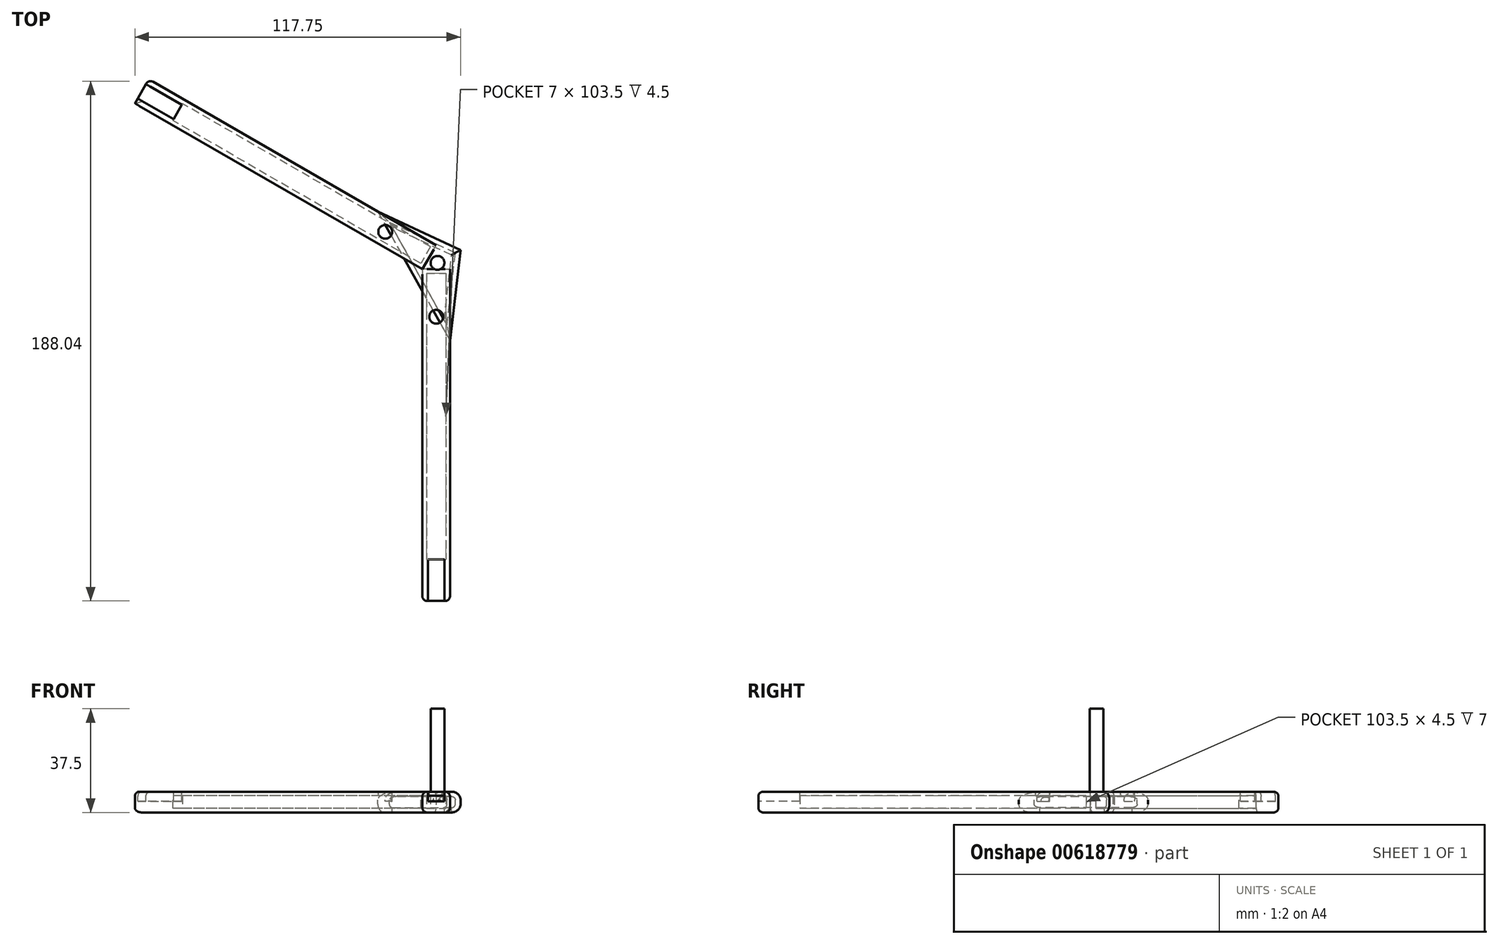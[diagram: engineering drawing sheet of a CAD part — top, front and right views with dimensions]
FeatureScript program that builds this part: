
annotation { "Feature Type Name" : "Feature", "Feature Type Description" : "" }
export const myFeature = defineFeature(function(context is Context, id is Id, definition is map)
    precondition{}
    {
        {
            var Q0;
            Q0=qCreatedBy(makeId("Top.planeOp"),FACE);
            var sketch = newSketch(context, id + "F0", { "sketchPlane" : qUnion([Q0])});
            skLineSegment(sketch, "E0.bottom", {"start": v(-40.03, 61.48) * mm, "end": v(-30.03, 61.48) * mm});
            skLineSegment(sketch, "E0.top", {"start": v(-40.03, -58.52) * mm, "end": v(-30.03, -58.52) * mm});
            skLineSegment(sketch, "E0.left", {"start": v(-40.03, 61.48) * mm, "end": v(-40.03, -58.52) * mm});
            skLineSegment(sketch, "E0.right", {"start": v(-30.03, 61.48) * mm, "end": v(-30.03, -58.52) * mm});
            skSolve(sketch);
        }
        {
            var Q0;
            Q0=makeQuery(id+"F0.imprint","IMPRINT",FACE,{"disambiguationData":[TD([[makeQuery(id+"F0.imprint","IMPRINT",EDGE,{"derivedFrom":sQuery(id+"F0.wireOp",EDGE,"E0.bottom")}),-1.0]])]});
            extrude(context, id + "F1", {"entities" : qUnion([Q0]), "depth" : 7.5 * mm, "offsetDistance" : 25 * mm});
        }
        {
            var Q0;
            Q0=makeQuery(id+"F1.opExtrude","SWEPT_BODY",BODY,{"disambiguationData":[OSD([sQuery(id+"F0.wireOp",EDGE,"E0.bottom"),sQuery(id+"F0.wireOp",EDGE,"E0.top"),sQuery(id+"F0.wireOp",EDGE,"E0.left"),sQuery(id+"F0.wireOp",EDGE,"E0.right")])]});
            var Q1;
            Q1=makeQuery(id+"F1.opExtrude","SWEPT_EDGE",EDGE,{"disambiguationData":[OSD([sQuery(id+"F0.wireOp",EDGE,"E0.bottom"),sQuery(id+"F0.wireOp",EDGE,"E0.left")])]});
            circularPattern(context, id + "F2", {"entities" : qUnion([Q0]), "axis" : qUnion([Q1]), "angle" : 120 * degree, "instanceCount" : 2, "equalSpace" : true});
        }
        {
            var Q0;
            Q0=makeQuery(id+"F2.opPattern","COPY",FACE,{"derivedFrom":makeQuery(id+"F1.opExtrude","CAP_FACE",FACE,{"disambiguationData":[OSD([sQuery(id+"F0.wireOp",EDGE,"E0.bottom"),sQuery(id+"F0.wireOp",EDGE,"E0.top"),sQuery(id+"F0.wireOp",EDGE,"E0.left"),sQuery(id+"F0.wireOp",EDGE,"E0.right")])],"isStart":false}),"instanceName":"1"});
            var sketch = newSketch(context, id + "F3", { "sketchPlane" : qUnion([Q0])});
            skSolve(sketch);
        }
        {
            var Q0;
            Q0 = qSketchRegion(id + "F3", true);
            var Q1;
            Q1=makeQuery(id+"F2.opPattern","COPY",FACE,{"derivedFrom":makeQuery(id+"F1.opExtrude","SWEPT_FACE",FACE,{"disambiguationData":[OSD([sQuery(id+"F0.wireOp",EDGE,"E0.left")])]}),"instanceName":"1"});
            extrude(context, id + "F4", {"entities" : qUnion([Q0, Q1]), "operationType" : NewBodyOperationType.ADD, "depth" : 10 * mm, "offsetDistance" : 25 * mm});
        }
        {
            var Q0;
            Q0=makeQuery(id+"F3.imprint","IMPRINT",FACE,{"disambiguationData":[TD([[makeQuery(id+"F3.imprint","IMPRINT",EDGE,{"derivedFrom":makeQuery(id+"F2.opPattern","COPY",EDGE,{"derivedFrom":makeQuery(id+"F1.opExtrude","CAP_EDGE",EDGE,{"disambiguationData":[OSD([sQuery(id+"F0.wireOp",EDGE,"E0.bottom")])],"isStart":false}),"instanceName":"1"})}),-1.0]])]});
            extrude(context, id + "F5", {"entities" : qUnion([Q0]), "operationType" : NewBodyOperationType.REMOVE, "endBound" : BoundingType.THROUGH_ALL, "oppositeDirection" : true, "depth" : 25 * mm, "offsetDistance" : 25 * mm});
        }
        {
            var Q0;
            Q0=makeQuery(id+"F1.opExtrude","CAP_FACE",FACE,{"disambiguationData":[OSD([sQuery(id+"F0.wireOp",EDGE,"E0.bottom"),sQuery(id+"F0.wireOp",EDGE,"E0.top"),sQuery(id+"F0.wireOp",EDGE,"E0.left"),sQuery(id+"F0.wireOp",EDGE,"E0.right")])],"isStart":false});
            var sketch = newSketch(context, id + "F6", { "sketchPlane" : qUnion([Q0])});
            skLineSegment(sketch, "E1", {"start": v(-30.03, 35.65) * mm, "end": v(-26.2, 68.43) * mm});
            skLineSegment(sketch, "E2", {"start": v(-26.2, 68.43) * mm, "end": v(-56.14, 82.33) * mm});
            skLineSegment(sketch, "E3", {"start": v(-56.14, 82.33) * mm, "end": v(-30.03, 35.65) * mm});
            skSolve(sketch);
        }
        {
            var Q0;
            Q0=makeQuery(id+"F1.opExtrude","SWEPT_FACE",FACE,{"disambiguationData":[OSD([sQuery(id+"F0.wireOp",EDGE,"E0.top")])]});
            shell(context, id + "F7", {"entities" : qUnion([Q0]), "thickness" : 1.5 * mm});
        }
        {
            var Q0;
            {var subQ0=sQuery(id+"F0.wireOp",EDGE,"E0.top");Q0=makeQuery(id+"F4.boolean.opBoolean","MERGE",FACE,{"derivedFrom":[makeQuery(id+"F2.opPattern","COPY",FACE,{"derivedFrom":makeQuery(id+"F1.opExtrude","SWEPT_FACE",FACE,{"disambiguationData":[OSD([subQ0])]}),"instanceName":"1"}),makeQuery(id+"F4.opExtrude","SWEPT_FACE",FACE,{"disambiguationData":[OSD([subQ0,sQuery(id+"F0.wireOp",EDGE,"E0.left")])]})]});}
            shell(context, id + "F8", {"entities" : qUnion([Q0]), "thickness" : 1.5 * mm});
        }
        {
            var Q0;
            {var subQ0=sQuery(id+"F0.wireOp",EDGE,"E0.top");Q0=makeQuery(id+"F4.boolean.opBoolean","MERGE",FACE,{"derivedFrom":[makeQuery(id+"F2.opPattern","COPY",FACE,{"derivedFrom":makeQuery(id+"F1.opExtrude","SWEPT_FACE",FACE,{"disambiguationData":[OSD([subQ0])]}),"instanceName":"1"}),makeQuery(id+"F4.opExtrude","SWEPT_FACE",FACE,{"disambiguationData":[OSD([subQ0,sQuery(id+"F0.wireOp",EDGE,"E0.left")])]})]});}
            var sketch = newSketch(context, id + "F9", { "sketchPlane" : qUnion([Q0])});
            skLineSegment(sketch, "E4", {"start": v(-41.73, 6) * mm, "end": v(-34.73, 6) * mm});
            skLineSegment(sketch, "E5", {"start": v(-34.73, 6) * mm, "end": v(-34.73, 1.5) * mm});
            skLineSegment(sketch, "E6", {"start": v(-34.73, 1.5) * mm, "end": v(-41.73, 1.5) * mm});
            skLineSegment(sketch, "E7", {"start": v(-41.73, 1.5) * mm, "end": v(-41.73, 6) * mm});
            skSolve(sketch);
        }
        {
            var Q0;
            Q0=makeQuery(id+"F9.imprint","IMPRINT",FACE,{"disambiguationData":[TD([[makeQuery(id+"F9.imprint","IMPRINT",EDGE,{"derivedFrom":sQuery(id+"F9.wireOp",EDGE,"E4")}),-1.0]])]});
            extrude(context, id + "F10", {"entities" : qUnion([Q0]), "operationType" : NewBodyOperationType.ADD, "oppositeDirection" : true, "depth" : 15 * mm, "offsetDistance" : 25 * mm});
        }
        {
            var Q0;
            Q0=makeQuery(id+"F1.opExtrude","SWEPT_FACE",FACE,{"disambiguationData":[OSD([sQuery(id+"F0.wireOp",EDGE,"E0.top")])]});
            var sketch = newSketch(context, id + "F11", { "sketchPlane" : qUnion([Q0])});
            skLineSegment(sketch, "E8", {"start": v(-38.53, 6) * mm, "end": v(-31.53, 6) * mm});
            skLineSegment(sketch, "E9", {"start": v(-31.53, 6) * mm, "end": v(-31.53, 1.5) * mm});
            skLineSegment(sketch, "E10", {"start": v(-31.53, 1.5) * mm, "end": v(-38.53, 1.5) * mm});
            skLineSegment(sketch, "E11", {"start": v(-38.53, 1.5) * mm, "end": v(-38.53, 6) * mm});
            skSolve(sketch);
        }
        {
            var Q0;
            Q0=makeQuery(id+"F11.imprint","IMPRINT",FACE,{"disambiguationData":[TD([[makeQuery(id+"F11.imprint","IMPRINT",EDGE,{"derivedFrom":sQuery(id+"F11.wireOp",EDGE,"E8")}),-1.0]])]});
            var Q1;
            Q1=makeQuery(id+"F11.imprint","IMPRINT",FACE,{"disambiguationData":[TD([[makeQuery(id+"F11.imprint","IMPRINT",EDGE,{"derivedFrom":sQuery(id+"F11.wireOp",EDGE,"E8")}),1.0]])]});
            extrude(context, id + "F12", {"entities" : qUnion([Q0, Q1]), "operationType" : NewBodyOperationType.ADD, "oppositeDirection" : true, "depth" : 15 * mm, "offsetDistance" : 25 * mm});
        }
        {
            var Q0;
            Q0=makeQuery(id+"F1.opExtrude","CAP_EDGE",EDGE,{"disambiguationData":[OSD([sQuery(id+"F0.wireOp",EDGE,"E0.left")])],"isStart":false});
            var Q1;
            Q1=makeQuery(id+"F1.opExtrude","CAP_EDGE",EDGE,{"disambiguationData":[OSD([sQuery(id+"F0.wireOp",EDGE,"E0.top")])],"isStart":false});
            var Q2;
            Q2=makeQuery(id+"F1.opExtrude","CAP_EDGE",EDGE,{"disambiguationData":[OSD([sQuery(id+"F0.wireOp",EDGE,"E0.right")])],"isStart":false});
            var Q3;
            {var subQ0=sQuery(id+"F0.wireOp",EDGE,"E0.left");Q3=makeQuery(id+"F4.opExtrude","CAP_EDGE",EDGE,{"disambiguationData":[OSD([subQ0]),TDD([makeQuery(id+"F2.opPattern","COPY",EDGE,{"derivedFrom":makeQuery(id+"F1.opExtrude","CAP_EDGE",EDGE,{"disambiguationData":[OSD([subQ0])],"isStart":false}),"instanceName":"1"})])],"isStart":false});}
            var Q4;
            Q4=makeQuery(id+"F5.boolean.opBoolean","COPY",EDGE,{"derivedFrom":makeQuery(id+"F5.opExtrude","CAP_EDGE",EDGE,{"disambiguationData":[OSD([sQuery(id+"F0.wireOp",EDGE,"E0.left")])],"isStart":true})});
            var Q5;
            {var subQ0=sQuery(id+"F0.wireOp",EDGE,"E0.left");var subQ1=sQuery(id+"F0.wireOp",EDGE,"E0.top");Q5=makeQuery(id+"F4.boolean.opBoolean","MERGE",EDGE,{"derivedFrom":[makeQuery(id+"F2.opPattern","COPY",EDGE,{"derivedFrom":makeQuery(id+"F1.opExtrude","CAP_EDGE",EDGE,{"disambiguationData":[OSD([subQ1])],"isStart":false}),"instanceName":"1"}),makeQuery(id+"F4.opExtrude","SWEPT_EDGE",EDGE,{"disambiguationData":[OSD([subQ1,subQ0]),TDD([makeQuery(id+"F2.opPattern","COPY",VERTEX,{"derivedFrom":makeQuery(id+"F1.opExtrude","CAP_VERTEX",VERTEX,{"disambiguationData":[OSD([subQ1,subQ0])],"isStart":false}),"instanceName":"1"})])]})]});}
            var Q6;
            Q6=makeQuery(id+"F5.boolean.opBoolean","COPY",EDGE,{"derivedFrom":makeQuery(id+"F5.opExtrude","SWEPT_EDGE",EDGE,{"disambiguationData":[OSD([sQuery(id+"F0.wireOp",EDGE,"E0.top"),sQuery(id+"F0.wireOp",EDGE,"E0.left")])]})});
            var Q7;
            Q7=makeQuery(id+"F4.opExtrude","CAP_EDGE",EDGE,{"disambiguationData":[OSD([sQuery(id+"F0.wireOp",EDGE,"E0.top"),sQuery(id+"F0.wireOp",EDGE,"E0.left")])],"isStart":false});
            var Q8;
            {var subQ0=sQuery(id+"F0.wireOp",EDGE,"E0.left");var subQ1=sQuery(id+"F0.wireOp",EDGE,"E0.top");Q8=makeQuery(id+"F4.boolean.opBoolean","MERGE",EDGE,{"derivedFrom":[makeQuery(id+"F2.opPattern","COPY",EDGE,{"derivedFrom":makeQuery(id+"F1.opExtrude","CAP_EDGE",EDGE,{"disambiguationData":[OSD([subQ1])],"isStart":true}),"instanceName":"1"}),makeQuery(id+"F4.opExtrude","SWEPT_EDGE",EDGE,{"disambiguationData":[OSD([subQ1,subQ0]),TDD([makeQuery(id+"F2.opPattern","COPY",VERTEX,{"derivedFrom":makeQuery(id+"F1.opExtrude","CAP_VERTEX",VERTEX,{"disambiguationData":[OSD([subQ1,subQ0])],"isStart":true}),"instanceName":"1"})])]})]});}
            var Q9;
            {var subQ0=sQuery(id+"F0.wireOp",EDGE,"E0.left");Q9=makeQuery(id+"F4.opExtrude","CAP_EDGE",EDGE,{"disambiguationData":[OSD([subQ0]),TDD([makeQuery(id+"F2.opPattern","COPY",EDGE,{"derivedFrom":makeQuery(id+"F1.opExtrude","CAP_EDGE",EDGE,{"disambiguationData":[OSD([subQ0])],"isStart":true}),"instanceName":"1"})])],"isStart":false});}
            var Q10;
            Q10=makeQuery(id+"F1.opExtrude","CAP_EDGE",EDGE,{"disambiguationData":[OSD([sQuery(id+"F0.wireOp",EDGE,"E0.right")])],"isStart":true});
            var Q11;
            Q11=makeQuery(id+"F1.opExtrude","CAP_EDGE",EDGE,{"disambiguationData":[OSD([sQuery(id+"F0.wireOp",EDGE,"E0.left")])],"isStart":true});
            var Q12;
            Q12=makeQuery(id+"F1.opExtrude","CAP_EDGE",EDGE,{"disambiguationData":[OSD([sQuery(id+"F0.wireOp",EDGE,"E0.top")])],"isStart":true});
            var Q13;
            Q13=makeQuery(id+"F1.opExtrude","SWEPT_EDGE",EDGE,{"disambiguationData":[OSD([sQuery(id+"F0.wireOp",EDGE,"E0.top"),sQuery(id+"F0.wireOp",EDGE,"E0.right")])]});
            var Q14;
            Q14=makeQuery(id+"F1.opExtrude","SWEPT_EDGE",EDGE,{"disambiguationData":[OSD([sQuery(id+"F0.wireOp",EDGE,"E0.top"),sQuery(id+"F0.wireOp",EDGE,"E0.left")])]});
            var Q15;
            {var subQ0=sQuery(id+"F0.wireOp",EDGE,"E0.left");Q15=makeQuery(id+"F5.boolean.opBoolean","INTERSECT",EDGE,{"derivedFrom":[makeQuery(id+"F4.boolean.opBoolean","MERGE",FACE,{"derivedFrom":[makeQuery(id+"F2.opPattern","COPY",FACE,{"derivedFrom":makeQuery(id+"F1.opExtrude","CAP_FACE",FACE,{"disambiguationData":[OSD([sQuery(id+"F0.wireOp",EDGE,"E0.bottom"),sQuery(id+"F0.wireOp",EDGE,"E0.top"),subQ0,sQuery(id+"F0.wireOp",EDGE,"E0.right")])],"isStart":true}),"instanceName":"1"}),makeQuery(id+"F4.opExtrude","SWEPT_FACE",FACE,{"disambiguationData":[OSD([subQ0]),TDD([makeQuery(id+"F2.opPattern","COPY",EDGE,{"derivedFrom":makeQuery(id+"F1.opExtrude","CAP_EDGE",EDGE,{"disambiguationData":[OSD([subQ0])],"isStart":true}),"instanceName":"1"})])]})]}),makeQuery(id+"F5.opExtrude","SWEPT_FACE",FACE,{"disambiguationData":[OSD([subQ0])]})]});}
            fillet(context, id + "F13", {"entities" : qUnion([Q0, Q1, Q2, Q3, Q4, Q5, Q6, Q7, Q8, Q9, Q10, Q11, Q12, Q13, Q14, Q15]), "radius" : 1.7 * mm, "tangentPropagation" : true, "allowEdgeOverflow" : false});
        }
        {
            var Q0;
            {var subQ5=sQuery(id+"F6.wireOp",EDGE,"E1");Q0=makeQuery(id+"F6.imprint","IMPRINT",FACE,{"disambiguationData":[TD([[makeQuery(id+"F6.imprint","IMPRINT",EDGE,{"derivedFrom":subQ5}),1.0]])]});}
            var Q1;
            {var subQ5=makeQuery(id+"F1.opExtrude","CAP_EDGE",EDGE,{"disambiguationData":[OSD([sQuery(id+"F0.wireOp",EDGE,"E0.bottom")])],"isStart":false});Q1=makeQuery(id+"F6.imprint","IMPRINT",FACE,{"disambiguationData":[TD([[makeQuery(id+"F6.imprint","IMPRINT",EDGE,{"derivedFrom":subQ5}),-1.0]])]});}
            extrude(context, id + "F14", {"entities" : qUnion([Q0, Q1]), "oppositeDirection" : true, "depth" : 7.5 * mm, "offsetDistance" : 25 * mm});
        }
        {
            var Q0;
            Q0=makeQuery(id+"F14.opExtrude","CAP_EDGE",EDGE,{"disambiguationData":[OSD([sQuery(id+"F6.wireOp",EDGE,"E1")])],"isStart":true});
            var Q1;
            Q1=makeQuery(id+"F14.opExtrude","CAP_EDGE",EDGE,{"disambiguationData":[OSD([sQuery(id+"F6.wireOp",EDGE,"E1")])],"isStart":false});
            var Q2;
            Q2=makeQuery(id+"F14.opExtrude","CAP_EDGE",EDGE,{"disambiguationData":[OSD([sQuery(id+"F6.wireOp",EDGE,"E2")])],"isStart":false});
            var Q3;
            Q3=makeQuery(id+"F14.opExtrude","CAP_EDGE",EDGE,{"disambiguationData":[OSD([sQuery(id+"F6.wireOp",EDGE,"E2")])],"isStart":true});
            var Q4;
            Q4=makeQuery(id+"F14.opExtrude","CAP_EDGE",EDGE,{"disambiguationData":[OSD([sQuery(id+"F6.wireOp",EDGE,"E3")])],"isStart":true});
            fillet(context, id + "F15", {"entities" : qUnion([Q0, Q1, Q2, Q3, Q4]), "radius" : 3 * mm, "tangentPropagation" : true, "allowEdgeOverflow" : false});
        }
        {
            var Q0;
            Q0=makeQuery(id+"F14.opExtrude","CAP_FACE",FACE,{"disambiguationData":[OSD([sQuery(id+"F6.wireOp",EDGE,"E1"),sQuery(id+"F6.wireOp",EDGE,"E2"),sQuery(id+"F6.wireOp",EDGE,"E3")])],"isStart":false});
            shell(context, id + "F16", {"entities" : qUnion([Q0]), "thickness" : 1.75 * mm});
        }
        {
            var Q0;
            Q0=makeQuery(id+"F14.opExtrude","CAP_FACE",FACE,{"disambiguationData":[OSD([sQuery(id+"F6.wireOp",EDGE,"E1"),sQuery(id+"F6.wireOp",EDGE,"E2"),sQuery(id+"F6.wireOp",EDGE,"E3")])],"isStart":true});
            var sketch = newSketch(context, id + "F17", { "sketchPlane" : qUnion([Q0])});
            skCircle(sketch, "E12", {"center": v(-34.54, 63.77) * mm, "radius": 2.5 * mm});
            skSolve(sketch);
        }
        {
            var Q0;
            Q0=makeQuery(id+"F17.imprint","IMPRINT",FACE,{"disambiguationData":[TD([[makeQuery(id+"F17.imprint","IMPRINT",EDGE,{"derivedFrom":sQuery(id+"F17.wireOp",EDGE,"E12")}),1.0]])]});
            extrude(context, id + "F18", {"entities" : qUnion([Q0]), "depth" : 30 * mm, "offsetDistance" : 25 * mm});
        }
        {
            var Q0;
            Q0=makeQuery(id+"F1.opExtrude","CAP_FACE",FACE,{"disambiguationData":[OSD([sQuery(id+"F0.wireOp",EDGE,"E0.bottom"),sQuery(id+"F0.wireOp",EDGE,"E0.top"),sQuery(id+"F0.wireOp",EDGE,"E0.left"),sQuery(id+"F0.wireOp",EDGE,"E0.right")])],"isStart":false});
            var sketch = newSketch(context, id + "F19", { "sketchPlane" : qUnion([Q0])});
            skLineSegment(sketch, "E13", {"start": v(-32.03, -58.52) * mm, "end": v(-32.03, -43.52) * mm});
            skLineSegment(sketch, "E14", {"start": v(-32.03, -43.52) * mm, "end": v(-38.03, -43.52) * mm});
            skLineSegment(sketch, "E15", {"start": v(-38.03, -43.52) * mm, "end": v(-38.03, -58.52) * mm});
            skLineSegment(sketch, "E16", {"start": v(-38.03, -58.52) * mm, "end": v(-32.03, -58.52) * mm});
            skSolve(sketch);
        }
        {
            var Q0;
            {var subQ0=sQuery(id+"F19.wireOp",EDGE,"E14");Q0=makeQuery(id+"F19.imprint","IMPRINT",FACE,{"disambiguationData":[TD([[makeQuery(id+"F19.imprint","IMPRINT",EDGE,{"derivedFrom":subQ0}),1.0]])]});}
            var Q1;
            {var subQ0=sQuery(id+"F19.wireOp",EDGE,"E16");Q1=makeQuery(id+"F19.imprint","IMPRINT",FACE,{"disambiguationData":[TD([[makeQuery(id+"F19.imprint","IMPRINT",EDGE,{"derivedFrom":subQ0}),1.0]])]});}
            extrude(context, id + "F20", {"entities" : qUnion([Q0, Q1]), "operationType" : NewBodyOperationType.REMOVE, "oppositeDirection" : true, "depth" : 3.5 * mm, "offsetDistance" : 25 * mm});
        }
        {
            var Q0;
            {var subQ0=sQuery(id+"F0.wireOp",EDGE,"E0.left");Q0=makeQuery(id+"F4.boolean.opBoolean","MERGE",FACE,{"derivedFrom":[makeQuery(id+"F2.opPattern","COPY",FACE,{"derivedFrom":makeQuery(id+"F1.opExtrude","CAP_FACE",FACE,{"disambiguationData":[OSD([sQuery(id+"F0.wireOp",EDGE,"E0.bottom"),sQuery(id+"F0.wireOp",EDGE,"E0.top"),subQ0,sQuery(id+"F0.wireOp",EDGE,"E0.right")])],"isStart":false}),"instanceName":"1"}),makeQuery(id+"F4.opExtrude","SWEPT_FACE",FACE,{"disambiguationData":[OSD([subQ0]),TDD([makeQuery(id+"F2.opPattern","COPY",EDGE,{"derivedFrom":makeQuery(id+"F1.opExtrude","CAP_EDGE",EDGE,{"disambiguationData":[OSD([subQ0])],"isStart":false}),"instanceName":"1"})])]})]});}
            var sketch = newSketch(context, id + "F21", { "sketchPlane" : qUnion([Q0])});
            skPoint(sketch, "E17", {"position": v(-142.09, 124.72) * mm});
            skLineSegment(sketch, "E18", {"start": v(-142.96, 123.22) * mm, "end": v(-129.97, 115.72) * mm});
            skLineSegment(sketch, "E19", {"start": v(-129.97, 115.72) * mm, "end": v(-126.97, 120.91) * mm});
            skLineSegment(sketch, "E20", {"start": v(-126.97, 120.91) * mm, "end": v(-139.96, 128.41) * mm});
            skLineSegment(sketch, "E21", {"start": v(-139.96, 128.41) * mm, "end": v(-142.96, 123.22) * mm});
            skSolve(sketch);
        }
        {
            var Q0;
            {var subQ0=sQuery(id+"F21.wireOp",EDGE,"E19");Q0=makeQuery(id+"F21.imprint","IMPRINT",FACE,{"disambiguationData":[TD([[makeQuery(id+"F21.imprint","IMPRINT",EDGE,{"derivedFrom":subQ0}),1.0]])]});}
            var Q1;
            {var subQ0=sQuery(id+"F21.wireOp",EDGE,"E21");Q1=makeQuery(id+"F21.imprint","IMPRINT",FACE,{"disambiguationData":[TD([[makeQuery(id+"F21.imprint","IMPRINT",EDGE,{"derivedFrom":subQ0}),1.0]])]});}
            extrude(context, id + "F22", {"entities" : qUnion([Q0, Q1]), "operationType" : NewBodyOperationType.REMOVE, "oppositeDirection" : true, "depth" : 3.5 * mm, "offsetDistance" : 25 * mm});
        }
        {
            var Q0;
            Q0=makeQuery(id+"F1.opExtrude","CAP_FACE",FACE,{"disambiguationData":[OSD([sQuery(id+"F0.wireOp",EDGE,"E0.bottom"),sQuery(id+"F0.wireOp",EDGE,"E0.top"),sQuery(id+"F0.wireOp",EDGE,"E0.left"),sQuery(id+"F0.wireOp",EDGE,"E0.right")])],"isStart":false});
            var sketch = newSketch(context, id + "F23", { "sketchPlane" : qUnion([Q0])});
            skCircle(sketch, "E22", {"center": v(-35.03, 44.28) * mm, "radius": 2.5 * mm});
            skSolve(sketch);
        }
        {
            var Q0;
            Q0=makeQuery(id+"F23.imprint","IMPRINT",FACE,{"disambiguationData":[TD([[makeQuery(id+"F23.imprint","IMPRINT",EDGE,{"derivedFrom":sQuery(id+"F23.wireOp",EDGE,"E22")}),1.0]])]});
            extrude(context, id + "F24", {"entities" : qUnion([Q0]), "operationType" : NewBodyOperationType.REMOVE, "oppositeDirection" : true, "depth" : 3.5 * mm, "offsetDistance" : 25 * mm});
        }
        {
            var Q0;
            {var subQ0=sQuery(id+"F0.wireOp",EDGE,"E0.left");Q0=makeQuery(id+"F4.boolean.opBoolean","MERGE",FACE,{"derivedFrom":[makeQuery(id+"F2.opPattern","COPY",FACE,{"derivedFrom":makeQuery(id+"F1.opExtrude","CAP_FACE",FACE,{"disambiguationData":[OSD([sQuery(id+"F0.wireOp",EDGE,"E0.bottom"),sQuery(id+"F0.wireOp",EDGE,"E0.top"),subQ0,sQuery(id+"F0.wireOp",EDGE,"E0.right")])],"isStart":false}),"instanceName":"1"}),makeQuery(id+"F4.opExtrude","SWEPT_FACE",FACE,{"disambiguationData":[OSD([subQ0]),TDD([makeQuery(id+"F2.opPattern","COPY",EDGE,{"derivedFrom":makeQuery(id+"F1.opExtrude","CAP_EDGE",EDGE,{"disambiguationData":[OSD([subQ0])],"isStart":false}),"instanceName":"1"})])]})]});}
            var sketch = newSketch(context, id + "F25", { "sketchPlane" : qUnion([Q0])});
            skCircle(sketch, "E23", {"center": v(-53.46, 75) * mm, "radius": 2.5 * mm});
            skSolve(sketch);
        }
        {
            var Q0;
            Q0=makeQuery(id+"F25.imprint","IMPRINT",FACE,{"disambiguationData":[TD([[makeQuery(id+"F25.imprint","IMPRINT",EDGE,{"derivedFrom":sQuery(id+"F25.wireOp",EDGE,"E23")}),1.0]])]});
            extrude(context, id + "F26", {"entities" : qUnion([Q0]), "operationType" : NewBodyOperationType.REMOVE, "oppositeDirection" : true, "depth" : 3.5 * mm, "offsetDistance" : 25 * mm});
        }
    });
